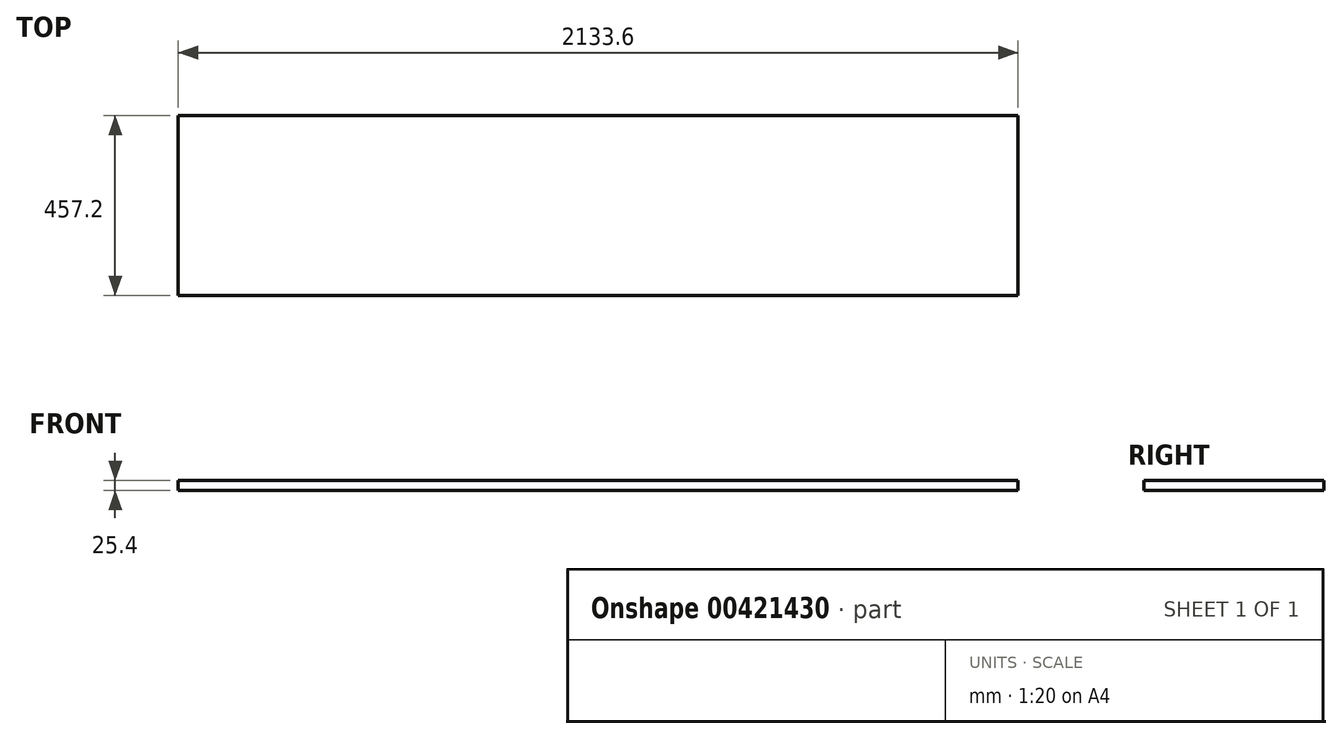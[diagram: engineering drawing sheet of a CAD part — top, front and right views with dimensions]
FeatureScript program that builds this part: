
annotation { "Feature Type Name" : "Feature", "Feature Type Description" : "" }
export const myFeature = defineFeature(function(context is Context, id is Id, definition is map)
    precondition{}
    {
        {
            var Q0;
            Q0=qCreatedBy(makeId("Top.planeOp"),FACE);
            var sketch = newSketch(context, id + "F0", { "sketchPlane" : qUnion([Q0])});
            skLineSegment(sketch, "E0.bottom", {"start": v(0, 0) * mm, "end": v(2133.6, 0) * mm});
            skLineSegment(sketch, "E0.top", {"start": v(0, 457.2) * mm, "end": v(2133.6, 457.2) * mm});
            skLineSegment(sketch, "E0.left", {"start": v(0, 0) * mm, "end": v(0, 457.2) * mm});
            skLineSegment(sketch, "E0.right", {"start": v(2133.6, 0) * mm, "end": v(2133.6, 457.2) * mm});
            skSolve(sketch);
        }
        {
            var Q0;
            Q0=makeQuery(id+"F0.imprint","IMPRINT",FACE,{"disambiguationData":[TD([[makeQuery(id+"F0.imprint","IMPRINT",EDGE,{"derivedFrom":sQuery(id+"F0.wireOp",EDGE,"E0.bottom")}),1.0]])]});
            extrude(context, id + "F1", {"entities" : qUnion([Q0]), "depth" : 25.4 * mm});
        }
    });
